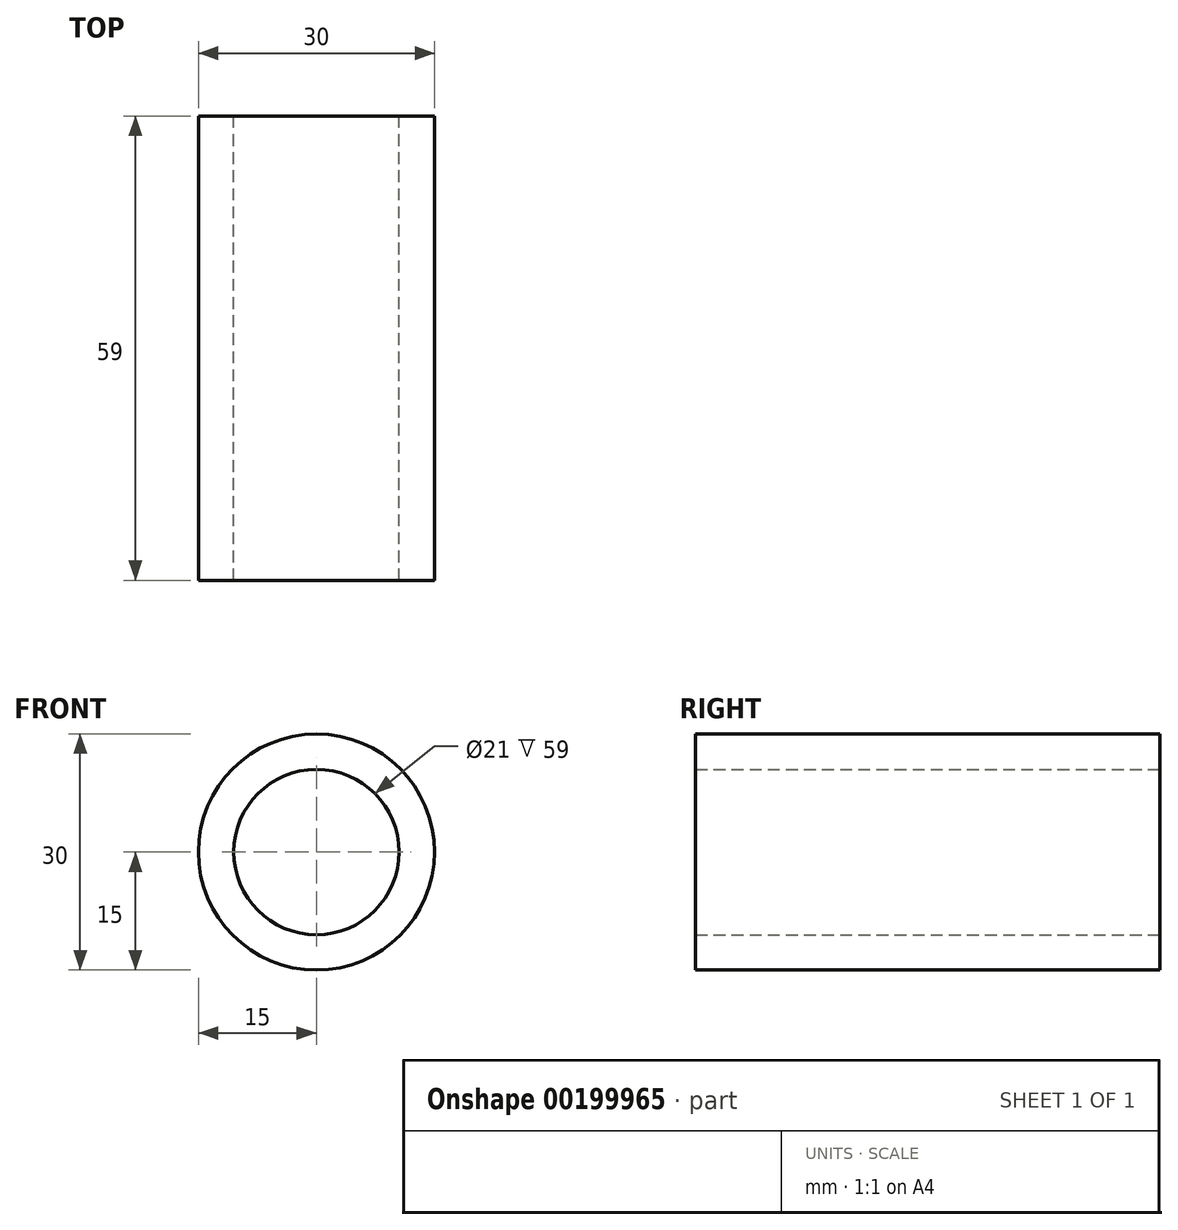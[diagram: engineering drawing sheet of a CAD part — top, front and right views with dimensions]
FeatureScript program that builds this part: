
annotation { "Feature Type Name" : "Feature", "Feature Type Description" : "" }
export const myFeature = defineFeature(function(context is Context, id is Id, definition is map)
    precondition{}
    {
        {
            var Q0;
            Q0=qCreatedBy(makeId("Front.planeOp"),FACE);
            var sketch = newSketch(context, id + "F0", { "sketchPlane" : qUnion([Q0])});
            skCircle(sketch, "E0", {"center": v(0, 0) * mm, "radius": 10.5 * mm});
            skCircle(sketch, "E1", {"center": v(0, 0) * mm, "radius": 15 * mm});
            skSolve(sketch);
        }
        {
            var Q0;
            Q0 = qSketchRegion(id + "F0", true);
            extrude(context, id + "F1", {"entities" : qUnion([Q0]), "depth" : 59 * mm});
        }
    });
